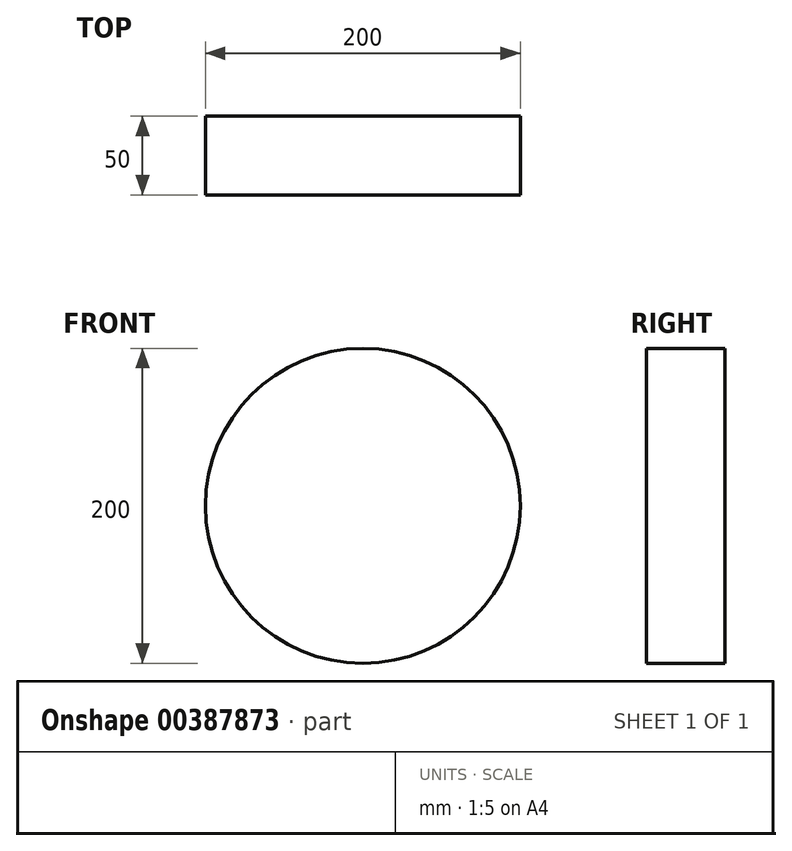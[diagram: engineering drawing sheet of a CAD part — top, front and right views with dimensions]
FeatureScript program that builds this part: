
annotation { "Feature Type Name" : "Feature", "Feature Type Description" : "" }
export const myFeature = defineFeature(function(context is Context, id is Id, definition is map)
    precondition{}
    {
        {
            var Q0;
            Q0=qCreatedBy(makeId("Front.planeOp"),FACE);
            var sketch = newSketch(context, id + "F0", { "sketchPlane" : qUnion([Q0])});
            skCircle(sketch, "E0", {"center": v(0, 0) * mm, "radius": 100 * mm});
            skSolve(sketch);
        }
        {
            var Q0;
            Q0=makeQuery(id+"F0.imprint","IMPRINT",FACE,{"disambiguationData":[TD([[makeQuery(id+"F0.imprint","IMPRINT",EDGE,{"derivedFrom":sQuery(id+"F0.wireOp",EDGE,"E0")}),1.0]])]});
            var Q1;
            Q1 = qSketchRegion(id + "F8lcOcWP7RNhk9P_0", true);
            extrude(context, id + "F1", {"entities" : qUnion([Q0, Q1]), "depth" : 50 * mm});
        }
    });
